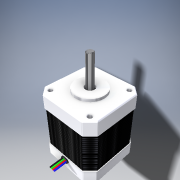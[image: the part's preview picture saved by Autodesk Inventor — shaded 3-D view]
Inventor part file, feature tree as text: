
AUTODESK INVENTOR PART (.ipt)
format: ipt  version: 2018 (Build 220112000, 112)  size: 1,108,992 bytes
history: native  units: mm
features: extrude x12, sketch x4, hole x4, fillet x4, chamfer x2, plane x1, pattern_linear x1, projected_geometry x1
ambient origin geometry x8: Origin, YZ Plane, XZ Plane, XY Plane, X Axis, Y Axis, Z Axis, Center Point
bodies: Solid1 (feature_tree)
feature tree (29):
  sketch  "Sketch1"  dims[d0=7.0mm d1=22.0mm]
  extrude  "Extrusion1"  Depth=22.0mm
  extrude  "Extrusion2"  Depth=31.0mm
  extrude  "Extrusion3"  Depth=3.0mm
  plane  "Work Plane2"
  extrude  "Extrusion7"  Depth=10.0mm
  extrude  "Extrusion8"  Depth=10.0mm
  chamfer  "Chamfer1"  Distance=42.0mm
  pattern_linear  "Rectangular Pattern2"  Spacing1=42.0mm  [1 undecoded]
  hole  "Hole1"  [1 undecoded]
  hole  "Hole2"  [1 undecoded]
  hole  "Hole3"  [1 undecoded]
  hole  "Hole4"  [1 undecoded]
  extrude  "Extrusion9"  Depth=10.0mm
  fillet  "Fillet1"  Radius=24.0mm
  fillet  "Fillet2"  Radius=2.0mm
  chamfer  "Chamfer2"  Distance=48.0mm
  fillet  "Fillet3"  [1 undecoded]
  sketch  "Sketch6"  dims[d10=3.0mm d11=3.0mm d12=3.0mm d39=42.0mm d40=42.0mm d41=135.0deg d42=51.618795mm d43=51.618795mm d44=25.809398mm d45=25.809398mm d46=24.0mm d47=0.0mm d48=2.0mm d49=0.0mm d50=48.0mm d51=0.0mm d60=-10.0mm d126=28.0mm d127=0.0mm d128=1.0mm d129=1.0mm d130=1.0mm d131=1.0mm d132=0.5mm d134=0.5mm d135=0.5mm d136=0.5mm d137=0.5mm d138=1.0mm d139=1.0mm d140=0.5mm d141=0.0mm d145=0.125mm d146=2.0mm d147=45.0deg d148=560.0mm d150=0.5mm d151=10.0mm d152=10.0mm d153=6.0mm d154=6.0mm d155=4.0mm d156=2.0mm d157=90.0deg d158=3.0mm d159=0.0mm d160=10.0mm d161=10.0mm d162=6.0mm d163=6.0mm d164=4.0mm d165=2.0mm d166=90.0deg d167=3.0mm d168=0.0mm d169=10.0mm d170=10.0mm d171=6.0mm d172=6.0mm d173=4.0mm d174=2.0mm d175=90.0deg d176=3.0mm d177=0.0mm d178=10.0mm d179=10.0mm d180=6.0mm d181=6.0mm d182=4.0mm d183=2.0mm d184=90.0deg d185=3.0mm d186=0.0mm d187=48.0mm d188=0.0mm d189=47.0mm d190=0.0mm d191=1.0mm d192=1.0mm d193=0.5mm d194=2.0mm d195=45.0deg d196=0.5mm d197=1.2mm d198=40.0mm d200=1.2mm d201=10.0mm d203=10.0mm d205=2.5mm d206=2.5mm d207=1.0mm d208=0.0mm d209=0.3mm d210=10.0mm d211=0.0mm d212=10.0mm d213=0.0mm d214=10.0mm d215=0.0mm d216=10.0mm d217=0.0mm d218=0.2mm d219=5.0mm d220=0.0mm d221=0.0mm]
  extrude  "Extrusion10"  Depth=10.0mm TaperAngle=0.0deg
  fillet  "Fillet4"  Radius=1.0mm
  extrude  "Extrusion11"  Depth=10.0mm
  extrude  "Extrusion12"  Depth=10.0mm
  extrude  "Extrusion13"  Depth=10.0mm
  extrude  "Extrusion14"  Depth=10.0mm
  extrude  "Extrusion15"  Depth=10.0mm
  sketch  "Sketch4"  dims[d4=5.0mm d5=31.0mm]
  projected_geometry  "Projected Loop2"
  sketch  "Sketch5"  dims[d6=31.0mm d9=3.0mm]
note: 6 required parameter values undecoded (feature->parameter linkage not recoverable at this tier; creation-order binding heuristic only, values carry confidence <= 0.55)
